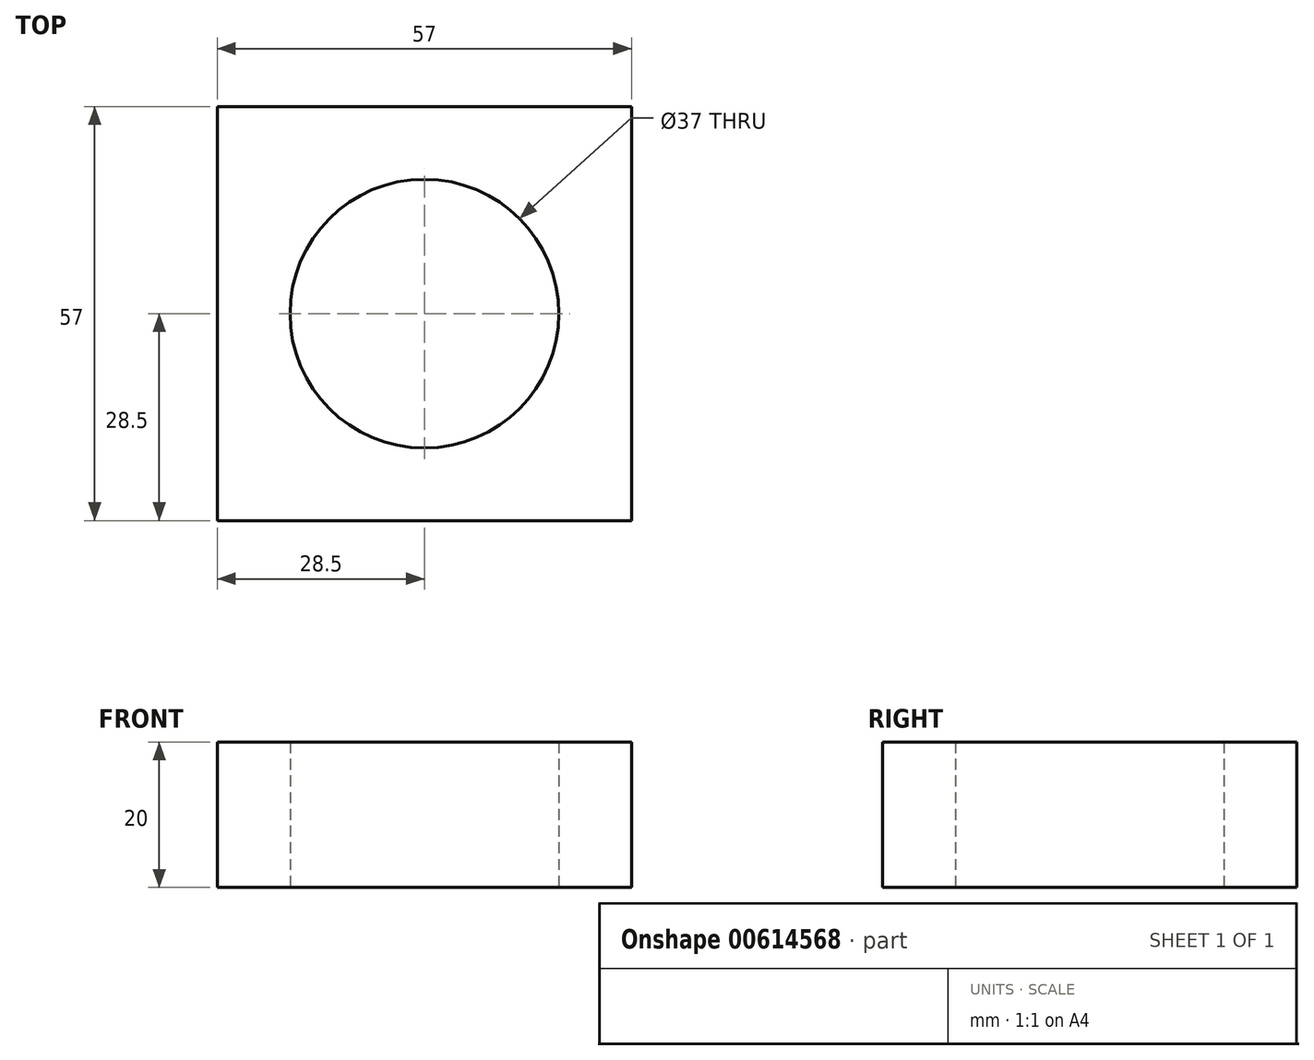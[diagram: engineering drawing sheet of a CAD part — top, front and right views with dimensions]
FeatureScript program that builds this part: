
annotation { "Feature Type Name" : "Feature", "Feature Type Description" : "" }
export const myFeature = defineFeature(function(context is Context, id is Id, definition is map)
    precondition{}
    {
        {
            assignVariable(context, id + "F0", {"name" : "HoleDepth", "anyValue" : 20});
        }
        {
            var Q0;
            Q0=qCreatedBy(makeId("Top.planeOp"),FACE);
            var sketch = newSketch(context, id + "F1", { "sketchPlane" : qUnion([Q0])});
            skLineSegment(sketch, "E0.bottom", {"start": v(28.5, 28.5) * mm, "end": v(-28.5, 28.5) * mm});
            skLineSegment(sketch, "E0.top", {"start": v(28.5, -28.5) * mm, "end": v(-28.5, -28.5) * mm});
            skLineSegment(sketch, "E0.left", {"start": v(28.5, 28.5) * mm, "end": v(28.5, -28.5) * mm});
            skLineSegment(sketch, "E0.right", {"start": v(-28.5, 28.5) * mm, "end": v(-28.5, -28.5) * mm});
            skPoint(sketch, "E0.middle", {"position": v(0, 0) * mm});
            skCircle(sketch, "E1", {"center": v(0, 0) * mm, "radius": 18.5 * mm});
            skSolve(sketch);
        }
        {
            var Q0;
            Q0 = qSketchRegion(id + "F1", true);
            extrude(context, id + "F2", {"entities" : qUnion([Q0]), "depth" : (getVariable(context, 'HoleDepth')) * mm, "offsetDistance" : 25 * mm});
        }
    });
